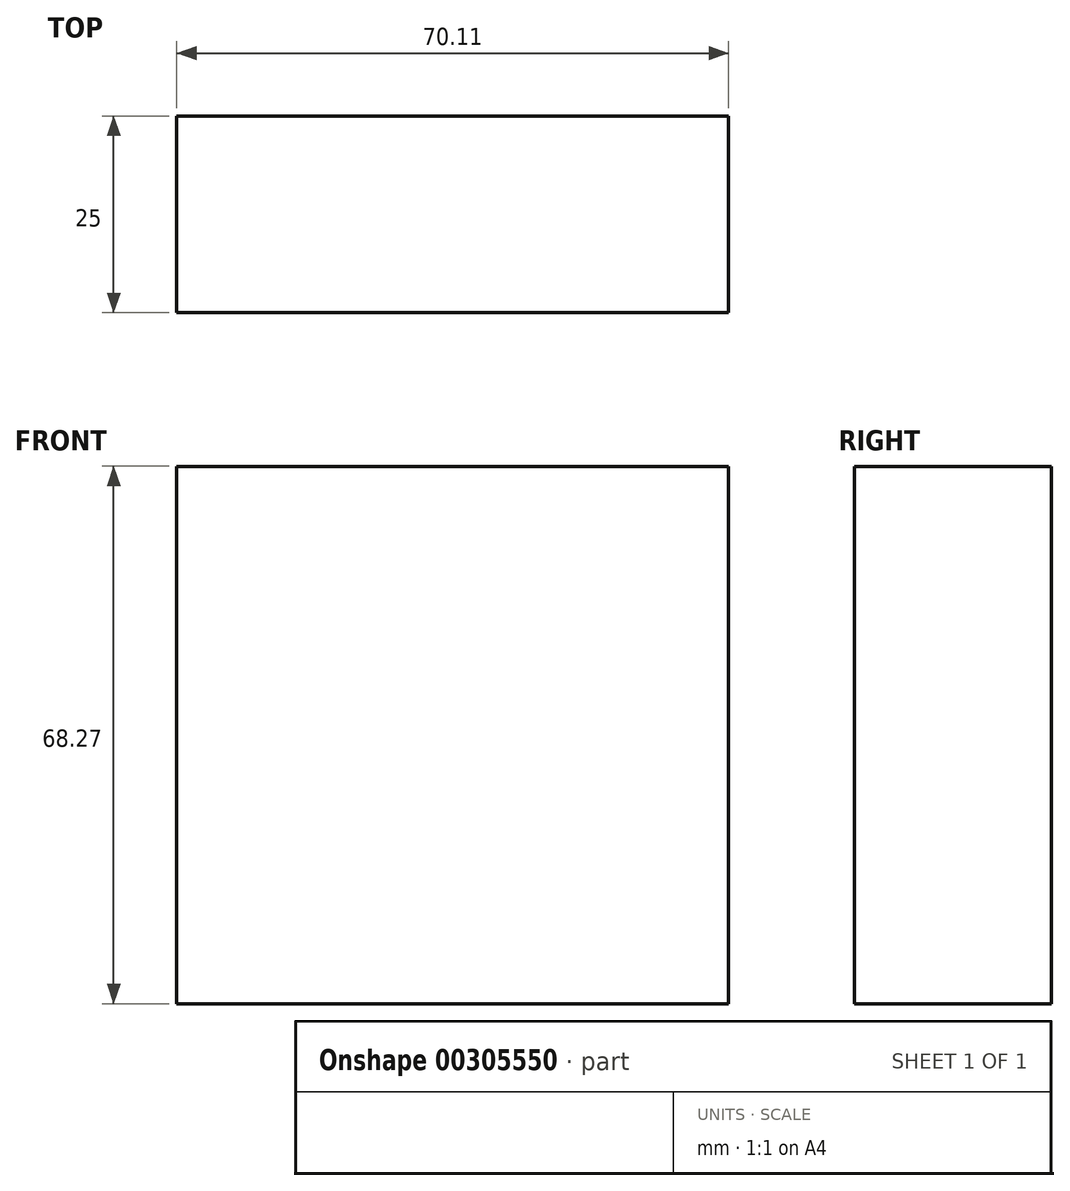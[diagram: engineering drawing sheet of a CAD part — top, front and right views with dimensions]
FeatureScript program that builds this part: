
annotation { "Feature Type Name" : "Feature", "Feature Type Description" : "" }
export const myFeature = defineFeature(function(context is Context, id is Id, definition is map)
    precondition{}
    {
        {
            var Q0;
            Q0=qCreatedBy(makeId("Front.planeOp"),FACE);
            var sketch = newSketch(context, id + "F0", { "sketchPlane" : qUnion([Q0])});
            skLineSegment(sketch, "E0.bottom", {"start": v(-100.29, 13.57) * mm, "end": v(-30.18, 13.57) * mm});
            skLineSegment(sketch, "E0.top", {"start": v(-100.29, 81.84) * mm, "end": v(-30.18, 81.84) * mm});
            skLineSegment(sketch, "E0.left", {"start": v(-100.29, 13.57) * mm, "end": v(-100.29, 81.84) * mm});
            skLineSegment(sketch, "E0.right", {"start": v(-30.18, 13.57) * mm, "end": v(-30.18, 81.84) * mm});
            skPoint(sketch, "E0.middle", {"position": v(-65.24, 47.7) * mm});
            skSolve(sketch);
        }
        {
            var Q0;
            Q0=makeQuery(id+"F0.imprint","IMPRINT",FACE,{"disambiguationData":[TD([[makeQuery(id+"F0.imprint","IMPRINT",EDGE,{"derivedFrom":sQuery(id+"F0.wireOp",EDGE,"E0.bottom")}),1.0]])]});
            extrude(context, id + "F1", {"entities" : qUnion([Q0]), "depth" : 25 * mm});
        }
    });
